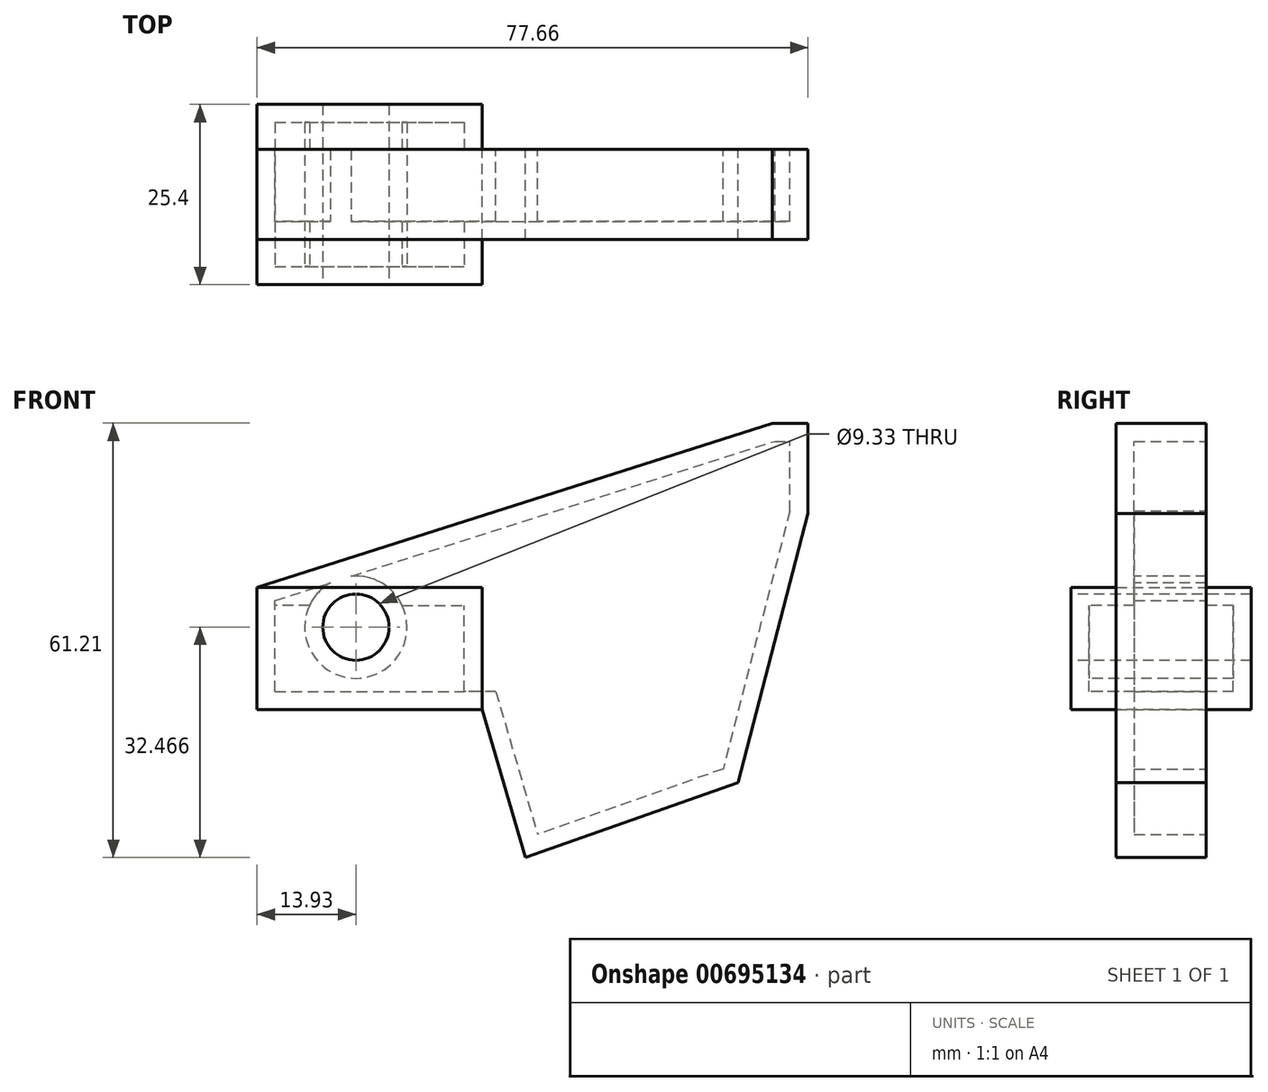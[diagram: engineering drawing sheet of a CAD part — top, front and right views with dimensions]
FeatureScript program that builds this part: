
annotation { "Feature Type Name" : "Feature", "Feature Type Description" : "" }
export const myFeature = defineFeature(function(context is Context, id is Id, definition is map)
    precondition{}
    {
        {
            var Q0;
            Q0=qCreatedBy(makeId("Front.planeOp"),FACE);
            var sketch = newSketch(context, id + "F0", { "sketchPlane" : qUnion([Q0])});
            skLineSegment(sketch, "E0.bottom", {"start": v(-39.92, -5.12) * mm, "end": v(-8.17, -5.12) * mm});
            skLineSegment(sketch, "E0.top", {"start": v(-39.92, 12.07) * mm, "end": v(-8.17, 12.07) * mm});
            skLineSegment(sketch, "E0.left", {"start": v(-39.92, -5.12) * mm, "end": v(-39.92, 12.07) * mm});
            skLineSegment(sketch, "E0.right", {"start": v(-8.17, -5.12) * mm, "end": v(-8.17, 12.07) * mm});
            skLineSegment(sketch, "E1.bottom", {"start": v(32.69, 22.5) * mm, "end": v(37.74, 22.5) * mm});
            skLineSegment(sketch, "E1.top", {"start": v(32.69, 35.2) * mm, "end": v(37.74, 35.2) * mm});
            skLineSegment(sketch, "E1.left", {"start": v(32.69, 22.5) * mm, "end": v(32.69, 35.2) * mm});
            skLineSegment(sketch, "E1.right", {"start": v(37.74, 22.5) * mm, "end": v(37.74, 35.2) * mm});
            skCircle(sketch, "E2.cCircle", {"center": v(9.87, -12.08) * mm, "radius": 9.17 * mm, "construction": true});
            skPoint(sketch, "E2.cCircle.perimeterSnap0", {"position": v(-24.04, -5.12) * mm});
            skLineSegment(sketch, "E2.0", {"start": v(3.78, 5.2) * mm, "end": v(27.89, -15.45) * mm});
            skLineSegment(sketch, "E2.1", {"start": v(27.89, -15.45) * mm, "end": v(-2.06, -26) * mm});
            skLineSegment(sketch, "E2.2", {"start": v(-2.06, -26) * mm, "end": v(3.78, 5.2) * mm});
            skPoint(sketch, "E2.0.midPoint", {"position": v(15.83, -5.12) * mm});
            skPoint(sketch, "E2.0.midPoint.positionSnap0", {"position": v(-24.04, -5.12) * mm});
            skLineSegment(sketch, "E3", {"start": v(32.69, 35.2) * mm, "end": v(3.78, 5.2) * mm});
            skLineSegment(sketch, "E4", {"start": v(37.74, 22.5) * mm, "end": v(27.89, -15.45) * mm});
            skLineSegment(sketch, "E5", {"start": v(-8.17, -5.12) * mm, "end": v(-2.06, -26) * mm});
            skLineSegment(sketch, "E6", {"start": v(-39.92, 12.07) * mm, "end": v(32.69, 35.2) * mm});
            skCircle(sketch, "E7", {"center": v(-25.99, 6.47) * mm, "radius": 4.66 * mm});
            skSolve(sketch);
        }
        {
            var Q0;
            Q0=makeQuery(id+"F0.imprint","IMPRINT",FACE,{"disambiguationData":[TD([[makeQuery(id+"F0.imprint","IMPRINT",EDGE,{"derivedFrom":sQuery(id+"F0.wireOp",EDGE,"E0.bottom")}),1.0]])]});
            extrude(context, id + "F1", {"entities" : qUnion([Q0]), "endBound" : BoundingType.SYMMETRIC, "oppositeDirection" : true, "depth" : 25.4 * mm, "offsetDistance" : 25.4 * mm});
        }
        {
            var Q0;
            Q0 = qSketchRegion(id + "F0", true);
            extrude(context, id + "F2", {"entities" : qUnion([Q0]), "operationType" : NewBodyOperationType.ADD, "endBound" : BoundingType.SYMMETRIC, "depth" : 12.7 * mm, "offsetDistance" : 25.4 * mm});
        }
        {
            var Q0;
            Q0=makeQuery(id+"F2.opExtrude","CAP_FACE",FACE,{"disambiguationData":[OSD([sQuery(id+"F0.wireOp",EDGE,"E0.bottom"),sQuery(id+"F0.wireOp",EDGE,"E0.left"),sQuery(id+"F0.wireOp",EDGE,"E1.top"),sQuery(id+"F0.wireOp",EDGE,"E1.right"),sQuery(id+"F0.wireOp",EDGE,"E2.1"),sQuery(id+"F0.wireOp",EDGE,"E4"),sQuery(id+"F0.wireOp",EDGE,"E5"),sQuery(id+"F0.wireOp",EDGE,"E6")])],"isStart":true});
            shell(context, id + "F3", {"entities" : qUnion([Q0]), "thickness" : 2.54 * mm});
        }
    });
